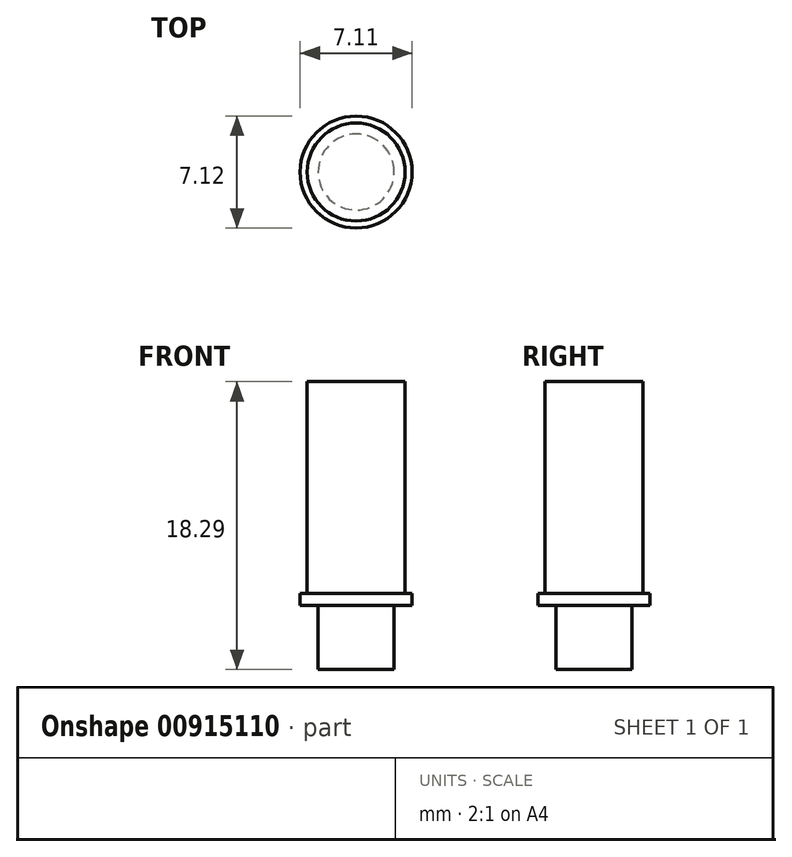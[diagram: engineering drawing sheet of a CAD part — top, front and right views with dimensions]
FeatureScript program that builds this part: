
annotation { "Feature Type Name" : "Feature", "Feature Type Description" : "" }
export const myFeature = defineFeature(function(context is Context, id is Id, definition is map)
    precondition{}
    {
        {
            var Q0;
            Q0=qCreatedBy(makeId("Top.planeOp"),FACE);
            var sketch = newSketch(context, id + "F0", { "sketchPlane" : qUnion([Q0])});
            skCircle(sketch, "E0", {"center": v(-47.52, 37.32) * mm, "radius": 2.41 * mm});
            skSolve(sketch);
        }
        {
            var Q0;
            Q0=makeQuery(id+"F0.imprint","IMPRINT",FACE,{"disambiguationData":[TD([[makeQuery(id+"F0.imprint","IMPRINT",EDGE,{"derivedFrom":sQuery(id+"F0.wireOp",EDGE,"E0")}),1.0]])]});
            extrude(context, id + "F1", {"entities" : qUnion([Q0]), "depth" : 4.06 * mm, "offsetDistance" : 25.4 * mm});
        }
        {
            var Q0;
            Q0=makeQuery(id+"F1.opExtrude","CAP_FACE",FACE,{"disambiguationData":[OSD([sQuery(id+"F0.wireOp",EDGE,"E0")])],"isStart":false});
            var sketch = newSketch(context, id + "F2", { "sketchPlane" : qUnion([Q0])});
            skCircle(sketch, "E1", {"center": v(-47.52, 37.32) * mm, "radius": 3.56 * mm});
            skSolve(sketch);
        }
        {
            var Q0;
            Q0=makeQuery(id+"F2.imprint","IMPRINT",FACE,{"disambiguationData":[TD([[makeQuery(id+"F2.imprint","IMPRINT",EDGE,{"derivedFrom":sQuery(id+"F2.wireOp",EDGE,"E1")}),1.0]])]});
            var Q1;
            Q1=makeQuery(id+"F2.imprint","IMPRINT",FACE,{"disambiguationData":[TD([[makeQuery(id+"F2.imprint","IMPRINT",EDGE,{"derivedFrom":makeQuery(id+"F1.opExtrude","CAP_EDGE",EDGE,{"disambiguationData":[OSD([sQuery(id+"F0.wireOp",EDGE,"E0")])],"isStart":false})}),1.0]])]});
            extrude(context, id + "F3", {"entities" : qUnion([Q0, Q1]), "operationType" : NewBodyOperationType.ADD, "depth" : 0.76 * mm, "offsetDistance" : 25.4 * mm});
        }
        {
            var Q0;
            Q0=makeQuery(id+"F3.opExtrude","CAP_FACE",FACE,{"disambiguationData":[OSD([sQuery(id+"F2.wireOp",EDGE,"E1")])],"isStart":false});
            var sketch = newSketch(context, id + "F4", { "sketchPlane" : qUnion([Q0])});
            skCircle(sketch, "E2", {"center": v(-47.52, 37.32) * mm, "radius": 3.11 * mm});
            skSolve(sketch);
        }
        {
            var Q0;
            Q0=makeQuery(id+"F4.imprint","IMPRINT",FACE,{"disambiguationData":[TD([[makeQuery(id+"F4.imprint","IMPRINT",EDGE,{"derivedFrom":sQuery(id+"F4.wireOp",EDGE,"E2")}),1.0]])]});
            extrude(context, id + "F5", {"entities" : qUnion([Q0]), "operationType" : NewBodyOperationType.ADD, "depth" : 13.46 * mm, "offsetDistance" : 25.4 * mm});
        }
    });
